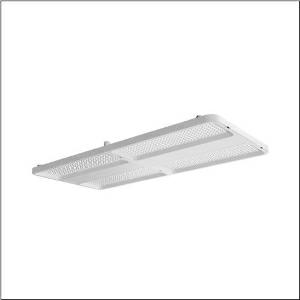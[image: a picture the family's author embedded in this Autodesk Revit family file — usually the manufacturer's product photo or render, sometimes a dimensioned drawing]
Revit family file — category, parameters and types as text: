
# Revit family: highbay_11_maxi_51hn12db4rda
name_source: partatom
category: Lighting Fixtures
units: mm (PartAtom-declared; Revit-internal decimal feet)

## family parameters
Cut with Voids When Loaded = No
Host = Face
Light Source = No
Part Type = Normal
Room Calculation Point = No
Round Connector Dimension = Use Diameter
Shared = No

## types (1)
- --- (1 x LED, 6720 lm, 32.8 W, 4000K)
    Apparent Load = 33 VA
    CIE Flux Codes = 87 98 100 100 100
    Color Rendering = 80
    Color Temperature = 4000K
    Default Elevation = 1800 mm
    Description = high bay luminaire Highbay 11 maxi; direct symmetric wide distribution, light control with lens of PMMA; UGR ≤ 22 (X = 4H | Y = 8H | S = 0.25H | reflection values 70/50/20); luminous flux: 42.500lm; light colour: 840, colour temperature: 4000K, MacAdam ≤ 2 SDCM (initial), colour rendering: CRI > 80; luminous efficacy: 198,9lm/W; rated service life: 100.000h (L95) at AT= 25°C; control: DALI 2; luminaire connection: terminal, 5-pole, max. 2.5mm² (cable entry for one cable, Ø 8.5..16mm); mains connection: 230..240V, AC/DC 0/50..60Hz; connected load: 213,7W; protection rating (complete): IP66; insulation class (complete): insulation class I (protective earthing); protection symbol: D; impact resistance: IK08; certification: CE, ENEC, VDE, UKCA; luminaire for central battery installations according to EN 60598-2-22, internal wiring halogen-free; luminaire Suitable for use in the food industry according to the specifications of IFS-Food, HACCP and/or BRC; LABS conformity tested according to VDMA 24364:2018-05; housing frame of high-performance plastic PA6, matt traffic white (RAL 9016); cover of PMMA; dimension (LxWxH): 946 x 442 x 72mm; permissible operating ambient temperature: -40..+50°C (reducing of maximum allowable ambient temperature of 5°C with ceiling mounting); packaging unit: 1 piece; (delivery without accessories; please order mounting accessories separately)
    Height = 72 mm  [stored 0.23622 ft]
    Lamp = 1 x LED
    Lamp Light Flux = 6720 lm
    Lamp Power = 32.8 W
    Lamp count = 1
    Length = 946 mm
    Luminous efficacy = 205 lm/W
    Manufacturer = Siteco
    ModVariant = No
    Model = 51HN12DB4RDA
    Mounting Place = Ceiling
    Mounting Type = Pendant
    Number of Poles = 1
    OnlyDefault = Yes
    Power Factor = 1
    Product Name = Highbay 11 maxi
    Product group = high bay luminaire
    ProductGroupID = 902
    Protection Class = Protection class I
    Protection Degree = IP 66
    RLX_Detail_Level = 1
    RLX_Emergency_Light_Flux = 0 lm
    RLX_Emergency_Type = 0
    RLX_Emergency_Type_DB = No
    RlxData = <blob elided: 127613 chars, md5=87ed4db4>
    Socket = socket
    Standby Power = 0 W
    System Light Flux = 6720 lm
    System Power = 33 W
    Type Comments = : DC mode (central or group accumulator) initial emergency light level
    Type Image = l_1363244.jpg
    URL = http://relux.com
    VarID = @adj_024883
    Voltage = 0 V
    Weight = 0.00 kg
    Width = 442 mm

note: [stored X ft] marks values corroborated as IEEE doubles in the binary element streams (Revit-internal decimal feet)

## geometry (parser evidence)
native form markers: Blend x4, Sweep x11
no freeform markers — native parametric forms only
